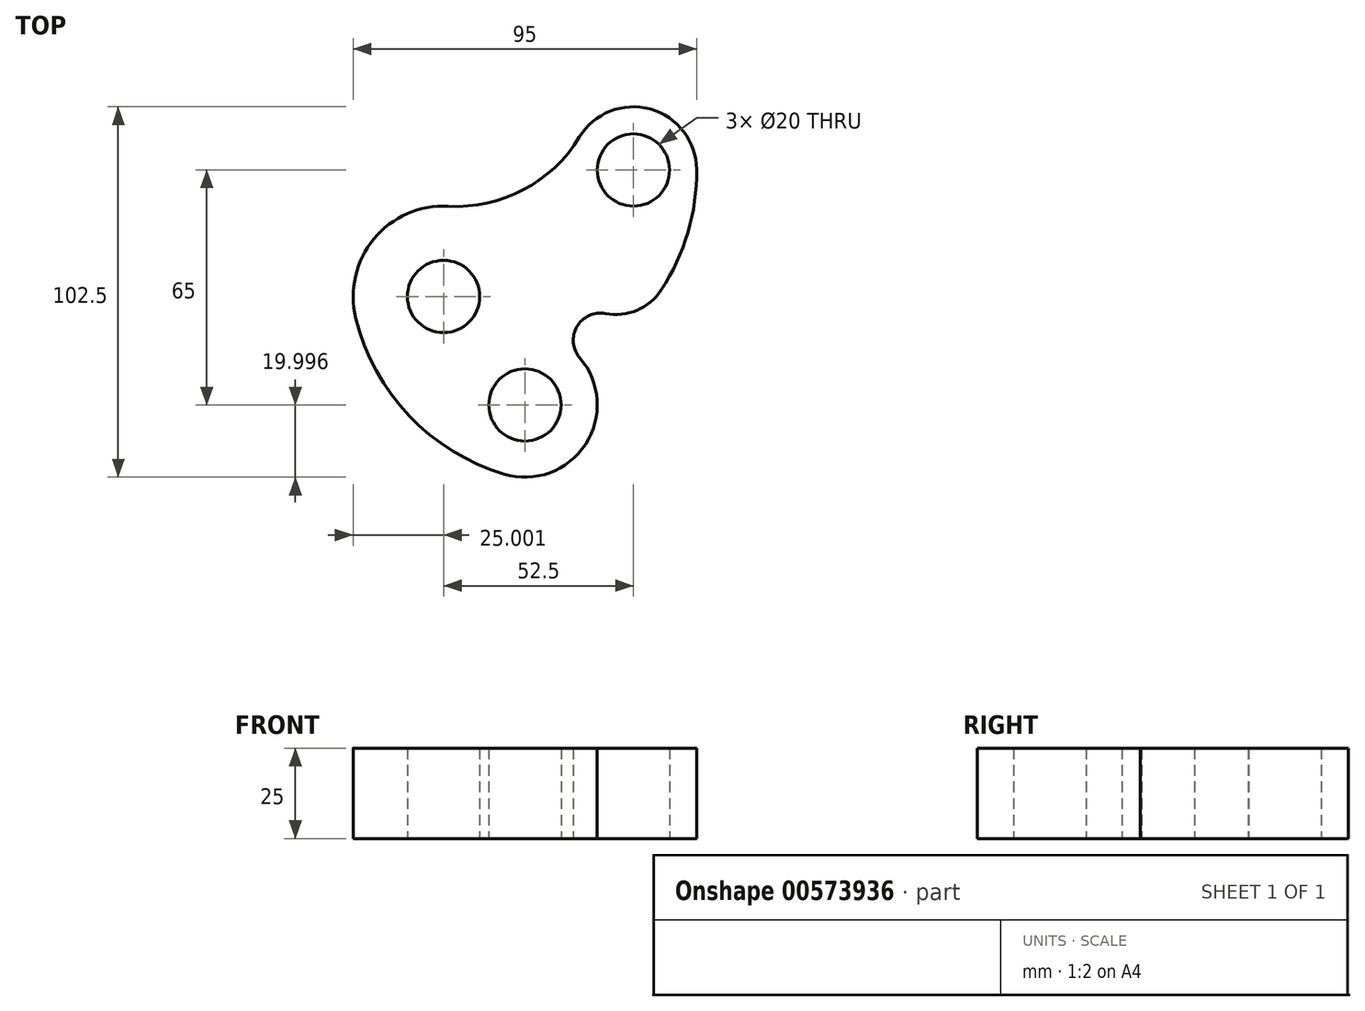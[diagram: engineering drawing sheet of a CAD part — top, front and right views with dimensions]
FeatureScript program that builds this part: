
annotation { "Feature Type Name" : "Feature", "Feature Type Description" : "" }
export const myFeature = defineFeature(function(context is Context, id is Id, definition is map)
    precondition{}
    {
        {
            var Q0;
            Q0=qCreatedBy(makeId("Top.planeOp"),FACE);
            var sketch = newSketch(context, id + "F0", { "sketchPlane" : qUnion([Q0])});
            skCircle(sketch, "E0", {"center": v(-37.68, 8.82) * mm, "radius": 10 * mm});
            skCircle(sketch, "E1", {"center": v(-15.18, -21.18) * mm, "radius": 10 * mm});
            skCircle(sketch, "E2", {"center": v(14.82, 43.82) * mm, "radius": 10 * mm});
            skArc(sketch, "E3", {"start": v(-36.37, 33.78) * mm, "mid": v(-56.93, 24.76) * mm, "end": v(-61.96, 2.88) * mm});
            skArc(sketch, "E4", {"start": v(32.32, 43.95) * mm, "mid": v(19.49, 60.68) * mm, "end": v(-0.13, 52.92) * mm});
            skArc(sketch, "E5", {"start": v(-36.37, 33.78) * mm, "mid": v(-15.61, 38.35) * mm, "end": v(-0.13, 52.92) * mm});
            skArc(sketch, "E6", {"start": v(-20.93, -40.34) * mm, "mid": v(1.59, -32.09) * mm, "end": v(0, -8.16) * mm});
            skArc(sketch, "E7", {"start": v(7.11, 4.09) * mm, "mid": v(15.79, 5) * mm, "end": v(22.5, 10.59) * mm});
            skArc(sketch, "E8", {"start": v(22.5, 10.59) * mm, "mid": v(29.88, 26.54) * mm, "end": v(32.32, 43.95) * mm});
            skArc(sketch, "E9", {"start": v(7.11, 4.09) * mm, "mid": v(-0.8, 0.49) * mm, "end": v(0, -8.16) * mm});
            skArc(sketch, "E10", {"start": v(-61.96, 2.88) * mm, "mid": v(-47.2, -24.19) * mm, "end": v(-20.93, -40.34) * mm});
            skSolve(sketch);
        }
        {
            var Q0;
            Q0=makeQuery(id+"F0.imprint","IMPRINT",FACE,{"disambiguationData":[TD([[makeQuery(id+"F0.imprint","IMPRINT",EDGE,{"derivedFrom":sQuery(id+"F0.wireOp",EDGE,"E0")}),-1.0]])]});
            extrude(context, id + "F1", {"entities" : qUnion([Q0]), "depth" : 25 * mm, "offsetDistance" : 25 * mm});
        }
    });
